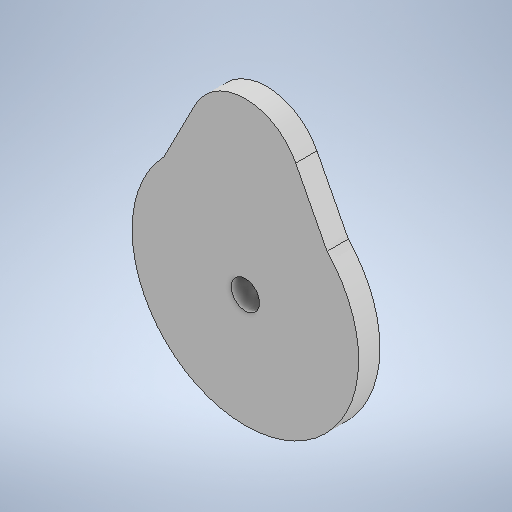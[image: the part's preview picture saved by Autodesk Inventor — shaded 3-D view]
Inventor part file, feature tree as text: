
AUTODESK INVENTOR PART (.ipt)
format: ipt  version: 2025 (Build 290162010, 162A)  size: 236,032 bytes
history: native  units: in
note: dims shown in document units (in); Inventor stores cm internally (conversion verified against a paired STEP export)
features: extrude x2, sketch x1
ambient origin geometry x8: Origin, YZ Plane, XZ Plane, XY Plane, X Axis, Y Axis, Z Axis, Center Point
bodies: Solid1 (feature_tree)
feature tree (3):
  extrude  "Extrusion1"  Depth=1.0in
  extrude  "Extrusion2"  Depth=1.0in
  sketch  "Sketch1"  dims[d0=2.0in d1=1.0in d2=1.0in d3=0.1875in d4=0.0in d5=0.25in d6=0.1875in d7=0.0in]
